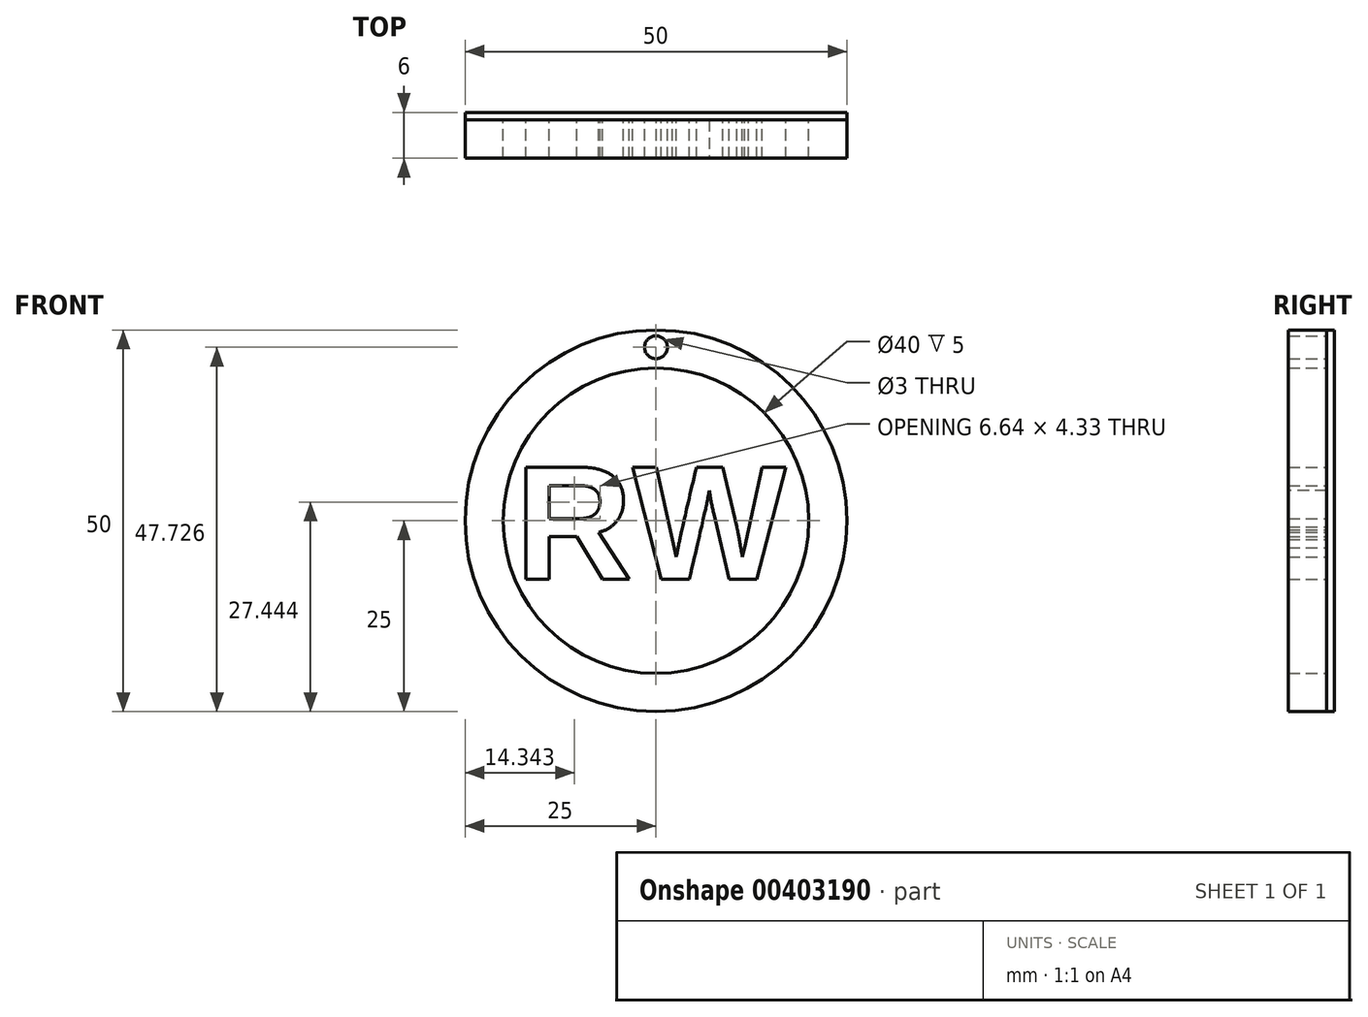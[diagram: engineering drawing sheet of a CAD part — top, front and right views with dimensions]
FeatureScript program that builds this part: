
annotation { "Feature Type Name" : "Feature", "Feature Type Description" : "" }
export const myFeature = defineFeature(function(context is Context, id is Id, definition is map)
    precondition{}
    {
        {
            var Q0;
            Q0=qCreatedBy(makeId("Front.planeOp"),FACE);
            var sketch = newSketch(context, id + "F0", { "sketchPlane" : qUnion([Q0])});
            skCircle(sketch, "E0", {"center": v(0, 0) * mm, "radius": 25 * mm});
            skCircle(sketch, "E1", {"center": v(0, 0) * mm, "radius": 20 * mm});
            skText(sketch, "E2", { "text": "RW", "fontName": "Arimo-Bold.ttf"});
            skCircle(sketch, "E3", {"center": v(0, 22.73) * mm, "radius": 1.5 * mm});
            const initialGuessF0  = {"E2": [-0.01847, -0.00767, 1, 0, 0.01534]};
            skSetInitialGuess(sketch, initialGuessF0);
            skSolve(sketch);
        }
        {
            var Q0;
            Q0=makeQuery(id+"F0.imprint","IMPRINT",FACE,{"disambiguationData":[TD([[makeQuery(id+"F0.imprint","IMPRINT",EDGE,{"derivedFrom":sQuery(id+"F0.wireOp",EDGE,"E2.sketch_text.stroke-0")}),-1.0]])]});
            var Q1;
            Q1=makeQuery(id+"F0.imprint","IMPRINT",FACE,{"disambiguationData":[TD([[makeQuery(id+"F0.imprint","IMPRINT",EDGE,{"derivedFrom":sQuery(id+"F0.wireOp",EDGE,"E2.sketch_text.stroke-18")}),-1.0]])]});
            var Q2;
            Q2=makeQuery(id+"F0.imprint","IMPRINT",FACE,{"disambiguationData":[TD([[makeQuery(id+"F0.imprint","IMPRINT",EDGE,{"derivedFrom":sQuery(id+"F0.wireOp",EDGE,"E0")}),1.0]])]});
            extrude(context, id + "F1", {"entities" : qUnion([Q0, Q1, Q2]), "depth" : 5 * mm});
        }
        {
            var Q0;
            Q0=qCreatedBy(makeId("Front.planeOp"),FACE);
            var sketch = newSketch(context, id + "F2", { "sketchPlane" : qUnion([Q0])});
            skCircle(sketch, "E4", {"center": v(0, 0) * mm, "radius": 25 * mm});
            skSolve(sketch);
        }
        {
            var Q0;
            Q0=makeQuery(id+"F2.imprint","IMPRINT",FACE,{"disambiguationData":[TD([[makeQuery(id+"F2.imprint","IMPRINT",EDGE,{"derivedFrom":sQuery(id+"F2.wireOp",EDGE,"E4")}),1.0]])]});
            extrude(context, id + "F3", {"entities" : qUnion([Q0]), "oppositeDirection" : true, "depth" : 1 * mm});
        }
    });
